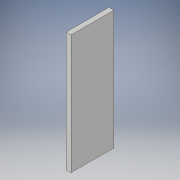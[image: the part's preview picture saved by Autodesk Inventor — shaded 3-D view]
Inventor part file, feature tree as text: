
AUTODESK INVENTOR PART (.ipt)
format: ipt  version: 2017 (Build 210142000, 142)  size: 90,624 bytes
history: native  units: in
note: dims shown in document units (in); Inventor stores cm internally (conversion verified against a paired STEP export)
features: extrude x1, sketch x1
ambient origin geometry x8: Origin, YZ Plane, XZ Plane, XY Plane, X Axis, Y Axis, Z Axis, Center Point
bodies: Solid1 (feature_tree)
feature tree (2):
  extrude  "Extrusion1"  Depth=4.345in
  sketch  "Sketch1"  dims[d0=12.085in d1=4.345in d2=0.5in d3=0.0in]
